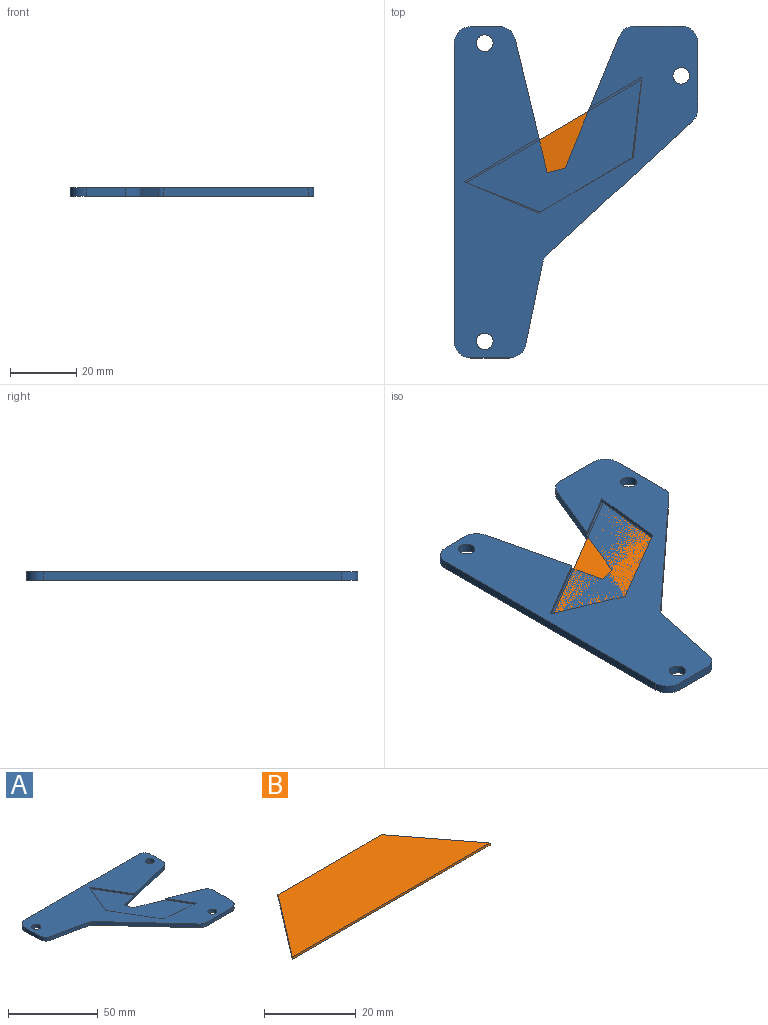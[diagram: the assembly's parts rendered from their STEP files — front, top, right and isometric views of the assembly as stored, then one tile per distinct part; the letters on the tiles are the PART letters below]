
ASSEMBLY  parts=2 mates=1
PART A: 29 faces, bbox 99.9x73.3x2.5 mm
  f0: plane 5.35x1.5mm, normal (0.97,0.23,0), area 8.2mm2, adj f3,f4,f22,f28
  f1: plane 14.05x2.5mm, normal (1,0,0), area 35.1mm2, adj f2,f20,f21,f22
  f2: cylinder r=5mm len=4.63mm, axis (0,0,-1), area 14.8mm2, adj f1,f3,f21,f22
  f3: plane 39.75x16.32mm, normal (0.38,0.93,0), area 87.7mm2, adj f0,f2,f21,f22,f23,f28
  f4: plane 40.19x9.6mm, normal (0.23,-0.97,0), area 92.5mm2, adj f0,f5,f21,f22,f25,f28
  f5: cylinder r=5mm len=4.92mm, axis (0,0,-1), area 16.9mm2, adj f4,f6,f21,f22
  f6: plane 8.53x2.5mm, normal (1,0.01,0), area 21.3mm2, adj f5,f7,f21,f22
  f7: cylinder r=5mm len=5mm, axis (0,0,-1), area 19.5mm2, adj f6,f8,f21,f22
  f8: plane 89.73x2.5mm, normal (0,1,0), area 224.3mm2, adj f7,f9,f21,f22
  f9: cylinder r=5mm len=5mm, axis (0,0,-1), area 19.6mm2, adj f8,f10,f21,f22
  f10: plane 11.64x2.5mm, normal (-1,0,0), area 29.1mm2, adj f9,f11,f21,f22
  f11: cylinder r=5mm len=4.9mm, axis (0,0,-1), area 17.1mm2, adj f10,f12,f21,f22
  f12: plane 24.51x5.07mm, normal (-0.2,-0.98,0), area 62.6mm2, adj f11,f13,f21,f22
  f13: cylinder r=5mm len=2.67mm, axis (0,0,-1), area 7.8mm2, adj f12,f14,f21,f22
  f14: plane 43.61x40.1mm, normal (-0.74,-0.68,0), area 148.1mm2, adj f13,f15,f21,f22
  f15: cylinder r=5mm len=3.68mm, axis (0,0,-1), area 10.3mm2, adj f14,f16,f21,f22
  f16: plane 20x2.5mm, normal (0,-1,0), area 50mm2, adj f15,f20,f21,f22
  f17: cylinder r=2.5mm len=5mm, axis (0,0,-1), area 39.3mm2, adj f21,f22
  f18: cylinder r=2.5mm len=5mm, axis (0,0,-1), area 39.3mm2, adj f21,f22
  f19: cylinder r=2.5mm len=5mm, axis (0,0,-1), area 39.3mm2, adj f21,f22
  f20: cylinder r=5mm len=5mm, axis (0,0,-1), area 19.6mm2, adj f1,f16,f21,f22
  f21: plane 99.94x73.35mm, normal (0,0,1), area 3131.4mm2, adj f1,f2,f3,f4,f5,f6,f7,f8
  f22: plane 99.94x73.35mm, normal (0,0,-1), area 3922.2mm2, adj f0,f1,f2,f3,f4,f5,f6,f7
  f23: plane 15.69x9.24mm, normal (-0.86,-0.51,0), area 18.2mm2, adj f3,f21,f24,f28
  f24: plane 24.16x2.59mm, normal (0.11,0.99,0), area 24.3mm2, adj f21,f23,f27,f28
  f25: plane 22.4x13.2mm, normal (-0.86,-0.51,0), area 26mm2, adj f4,f21,f26,f28
  f26: plane 22.39x9.44mm, normal (0.92,-0.39,0), area 24.3mm2, adj f21,f25,f27,f28
  f27: plane 28.43x16.75mm, normal (0.86,0.51,0), area 33mm2, adj f21,f24,f26,f28
  f28: plane 53.42x40.92mm, normal (0,0,1), area 790.9mm2, adj f0,f3,f4,f23,f24,f25,f26,f27
PART B: 6 faces, bbox 61x18.9x0.6 mm
  f0: plane 32.1x0.6mm, normal (0,1,0), area 19.3mm2, adj f1,f3,f4,f5
  f1: plane 18.9x14.45mm, normal (-0.79,0.61,0), area 14.3mm2, adj f0,f2,f4,f5
  f2: plane 61x0.6mm, normal (0,-1,0), area 36.6mm2, adj f1,f3,f4,f5
  f3: plane 18.9x14.45mm, normal (0.79,0.61,0), area 14.3mm2, adj f0,f2,f4,f5
  f4: plane 61x18.9mm, normal (0,0,1), area 879.8mm2, adj f0,f1,f2,f3
  f5: plane 61x18.9mm, normal (0,0,-1), area 879.8mm2, adj f0,f1,f2,f3
PLACE A rot(axis=(0,0,1),90deg) t=(7.48,67.33,-5.7)mm
PLACE B rot(axis=(0,0,-1),149.5deg) t=(-21.39,10,-4.8)mm
MATE pin_slot A.f28 <-> B.f4  axis (0,0,1) through (-9.33,7.92,-4.2)mm
